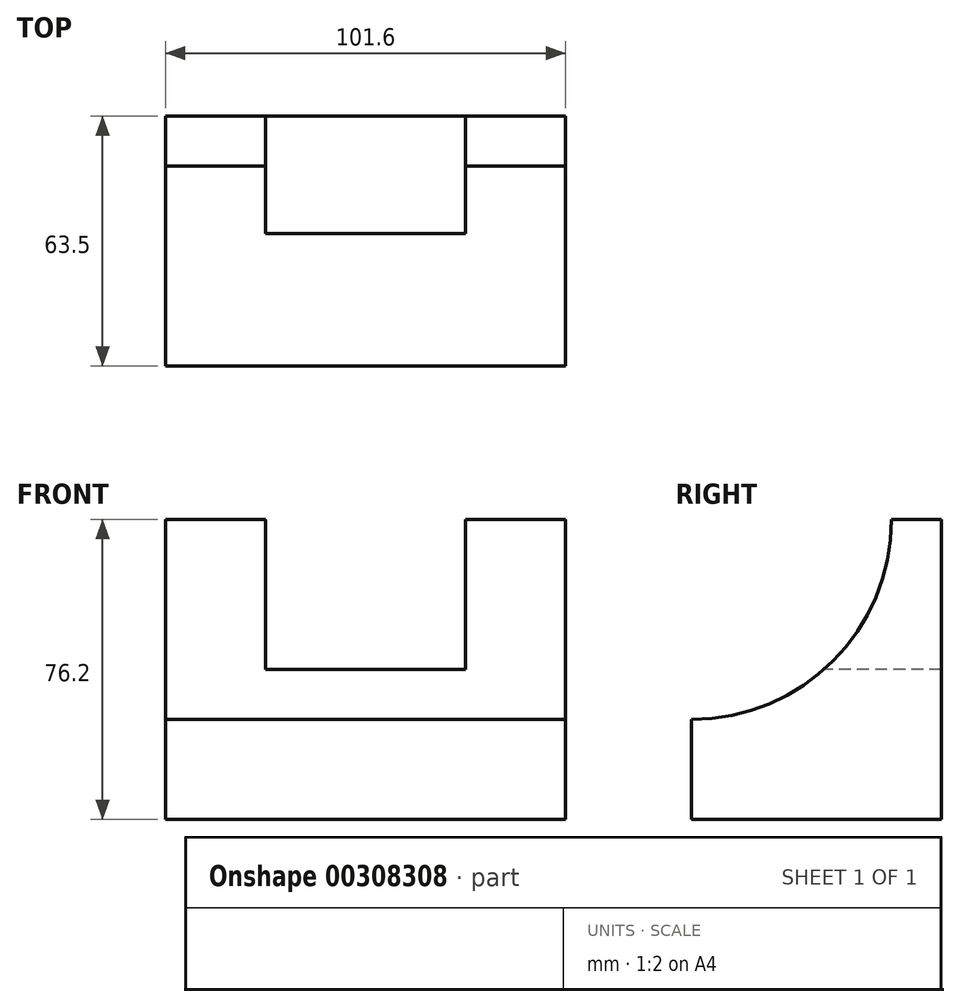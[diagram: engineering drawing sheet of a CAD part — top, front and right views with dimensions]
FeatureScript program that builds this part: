
annotation { "Feature Type Name" : "Feature", "Feature Type Description" : "" }
export const myFeature = defineFeature(function(context is Context, id is Id, definition is map)
    precondition{}
    {
        {
            var Q0;
            Q0=qCreatedBy(makeId("Right.planeOp"),FACE);
            var sketch = newSketch(context, id + "F0", { "sketchPlane" : qUnion([Q0])});
            skLineSegment(sketch, "E0", {"start": v(-29.76, -23.83) * mm, "end": v(33.74, -23.83) * mm});
            skLineSegment(sketch, "E1", {"start": v(33.74, -23.83) * mm, "end": v(33.74, 52.37) * mm});
            skLineSegment(sketch, "E2", {"start": v(33.74, 52.37) * mm, "end": v(-29.76, 52.37) * mm});
            skLineSegment(sketch, "E3", {"start": v(-29.76, 52.37) * mm, "end": v(-29.76, -23.83) * mm});
            skSolve(sketch);
        }
        {
            var Q0;
            Q0=makeQuery(id+"F0.imprint","IMPRINT",FACE,{"disambiguationData":[TD([[makeQuery(id+"F0.imprint","IMPRINT",EDGE,{"derivedFrom":sQuery(id+"F0.wireOp",EDGE,"E0")}),1.0]])]});
            extrude(context, id + "F1", {"entities" : qUnion([Q0]), "oppositeDirection" : true, "depth" : 101.6 * mm});
        }
        {
            var Q0;
            Q0=makeQuery(id+"F1.opExtrude","CAP_FACE",FACE,{"disambiguationData":[OSD([sQuery(id+"F0.wireOp",EDGE,"E0"),sQuery(id+"F0.wireOp",EDGE,"E1"),sQuery(id+"F0.wireOp",EDGE,"E2"),sQuery(id+"F0.wireOp",EDGE,"E3")])],"isStart":true});
            var sketch = newSketch(context, id + "F2", { "sketchPlane" : qUnion([Q0])});
            skCircle(sketch, "E4", {"center": v(-29.76, 52.37) * mm, "radius": 50.8 * mm});
            skSolve(sketch);
        }
        {
            var Q0;
            Q0=makeQuery(id+"F1.opExtrude","SWEPT_FACE",FACE,{"disambiguationData":[OSD([sQuery(id+"F0.wireOp",EDGE,"E3")])]});
            var sketch = newSketch(context, id + "F3", { "sketchPlane" : qUnion([Q0])});
            skLineSegment(sketch, "E5.bottom", {"start": v(-76.2, 52.37) * mm, "end": v(-25.4, 52.37) * mm});
            skLineSegment(sketch, "E5.top", {"start": v(-76.2, 14.27) * mm, "end": v(-25.4, 14.27) * mm});
            skLineSegment(sketch, "E5.left", {"start": v(-76.2, 52.37) * mm, "end": v(-76.2, 14.27) * mm});
            skLineSegment(sketch, "E5.right", {"start": v(-25.4, 52.37) * mm, "end": v(-25.4, 14.27) * mm});
            skLineSegment(sketch, "E6", {"start": v(-76.2, 52.37) * mm, "end": v(-101.6, 52.37) * mm});
            skLineSegment(sketch, "E7", {"start": v(-25.4, 52.37) * mm, "end": v(0, 52.37) * mm});
            skSolve(sketch);
        }
        {
            var Q0;
            Q0=makeQuery(id+"F3.imprint","IMPRINT",FACE,{"disambiguationData":[TD([[makeQuery(id+"F3.imprint","IMPRINT",EDGE,{"derivedFrom":sQuery(id+"F3.wireOp",EDGE,"E5.bottom")}),-1.0]])]});
            extrude(context, id + "F4", {"entities" : qUnion([Q0]), "operationType" : NewBodyOperationType.REMOVE, "endBound" : BoundingType.THROUGH_ALL, "oppositeDirection" : true, "depth" : 25.4 * mm});
        }
        {
            var Q0;
            {var subQ0=sQuery(id+"F2.wireOp",EDGE,"E4");var subQ1=makeQuery(id+"F1.opExtrude","CAP_EDGE",EDGE,{"disambiguationData":[OSD([sQuery(id+"F0.wireOp",EDGE,"E2")])],"isStart":true});var subQ2=makeQuery(id+"F2.imprint","INTERSECT",VERTEX,{"derivedFrom":[subQ1,subQ0]});Q0=makeQuery(id+"F2.imprint","IMPRINT",FACE,{"disambiguationData":[TD([[makeQuery(id+"F2.imprint","IMPRINT",EDGE,{"disambiguationData":[TD([[subQ2,-1.0]])],"derivedFrom":subQ0}),1.0]])]});}
            var Q1;
            {var subQ0=sQuery(id+"F2.wireOp",EDGE,"E4");var subQ1=makeQuery(id+"F1.opExtrude","CAP_EDGE",EDGE,{"disambiguationData":[OSD([sQuery(id+"F0.wireOp",EDGE,"E2")])],"isStart":true});var subQ2=makeQuery(id+"F2.imprint","INTERSECT",VERTEX,{"derivedFrom":[subQ1,subQ0]});Q1=makeQuery(id+"F2.imprint","IMPRINT",FACE,{"disambiguationData":[TD([[makeQuery(id+"F2.imprint","IMPRINT",EDGE,{"disambiguationData":[TD([[subQ2,1.0]])],"derivedFrom":subQ0}),1.0]])]});}
            extrude(context, id + "F5", {"entities" : qUnion([Q0, Q1]), "operationType" : NewBodyOperationType.REMOVE, "endBound" : BoundingType.THROUGH_ALL, "oppositeDirection" : true, "depth" : 25.4 * mm});
        }
    });
